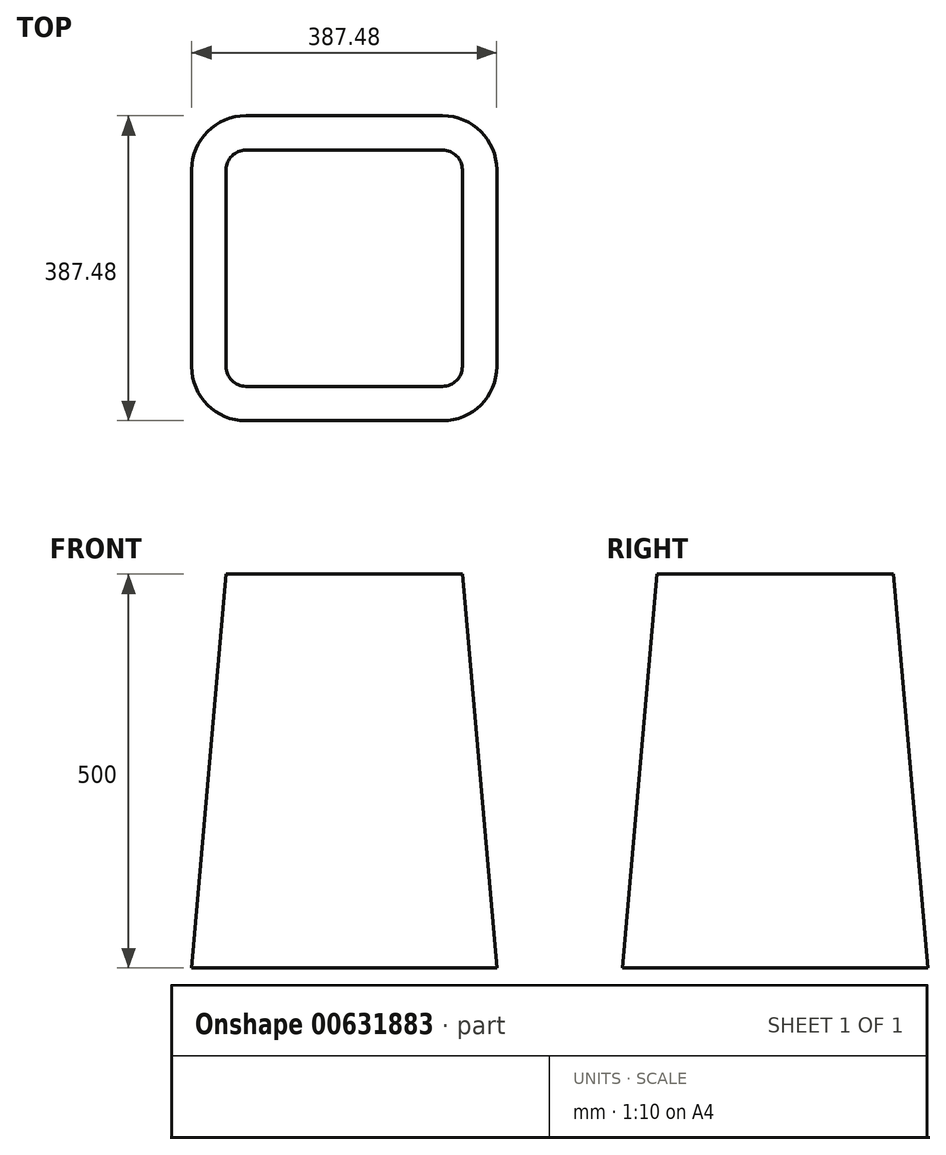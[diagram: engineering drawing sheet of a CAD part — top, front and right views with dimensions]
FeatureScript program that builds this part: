
annotation { "Feature Type Name" : "Feature", "Feature Type Description" : "" }
export const myFeature = defineFeature(function(context is Context, id is Id, definition is map)
    precondition{}
    {
        {
            var Q0;
            Q0=qCreatedBy(makeId("Top.planeOp"),FACE);
            var sketch = newSketch(context, id + "F0", { "sketchPlane" : qUnion([Q0])});
            skLineSegment(sketch, "E0.bottom", {"start": v(-125, -150) * mm, "end": v(125, -150) * mm});
            skLineSegment(sketch, "E0.top", {"start": v(-125, 150) * mm, "end": v(125, 150) * mm});
            skLineSegment(sketch, "E0.left", {"start": v(-150, -125) * mm, "end": v(-150, 125) * mm});
            skLineSegment(sketch, "E0.right", {"start": v(150, -125) * mm, "end": v(150, 125) * mm});
            skPoint(sketch, "E0.middle", {"position": v(0, 0) * mm});
            skPoint(sketch, "E1.visualSharp", {"position": v(-150, 150) * mm});
            skArc(sketch, "E1.filletArc", {"start": v(-125, 150) * mm, "mid": v(-142.68, 142.68) * mm, "end": v(-150, 125) * mm});
            skPoint(sketch, "E2.visualSharp", {"position": v(150, 150) * mm});
            skArc(sketch, "E2.filletArc", {"start": v(150, 125) * mm, "mid": v(142.68, 142.68) * mm, "end": v(125, 150) * mm});
            skPoint(sketch, "E3.visualSharp", {"position": v(150, -150) * mm});
            skArc(sketch, "E3.filletArc", {"start": v(125, -150) * mm, "mid": v(142.68, -142.68) * mm, "end": v(150, -125) * mm});
            skPoint(sketch, "E4.visualSharp", {"position": v(-150, -150) * mm});
            skArc(sketch, "E4.filletArc", {"start": v(-150, -125) * mm, "mid": v(-142.68, -142.68) * mm, "end": v(-125, -150) * mm});
            skSolve(sketch);
        }
        {
            var Q0;
            Q0 = qSketchRegion(id + "F0", true);
            extrude(context, id + "F1", {"entities" : qUnion([Q0]), "oppositeDirection" : true, "depth" : 500 * mm, "offsetDistance" : 25 * mm, "hasDraft" : true, "draftAngle" : 5 * degree});
        }
    });
